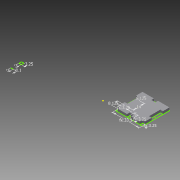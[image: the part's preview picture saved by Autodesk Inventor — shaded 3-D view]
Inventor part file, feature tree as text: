
AUTODESK INVENTOR PART (.ipt)
format: ipt  version: 2013 (Build 170138000, 138)  size: 126,976 bytes
history: native  units: mm
features: extrude x4, other x2, sketch x1
ambient origin geometry x8: Origin, YZ Plane, XZ Plane, XY Plane, X Axis, Y Axis, Z Axis, Center Point
feature tree (7):
  other  "Blocks"
  sketch  "Sketch1"  dims[d0=3.0mm d2=3.0mm d3=0.1mm d7=22.5mm d8=12.4mm d9=4.5mm d10=4.5mm d11=2.0mm d12=2.0mm d32=33.5mm d34=3.25mm d35=14.0mm d36=8.125mm d37=3.25mm d38=0.0mm d39=5.0mm d40=3.25mm d45=8.125mm d46=3.25mm d47=3.25mm d48=0.0mm d49=3.25mm d50=0.0mm d51=3.25mm d52=0.0mm]
  extrude  "Extrusion3"  Depth=3.0mm
  extrude  "Extrusion6"  Depth=33.5mm
  extrude  "Extrusion7"  Depth=3.25mm
  extrude  "Extrusion8"  Depth=14.0mm
  other  "Block1"
